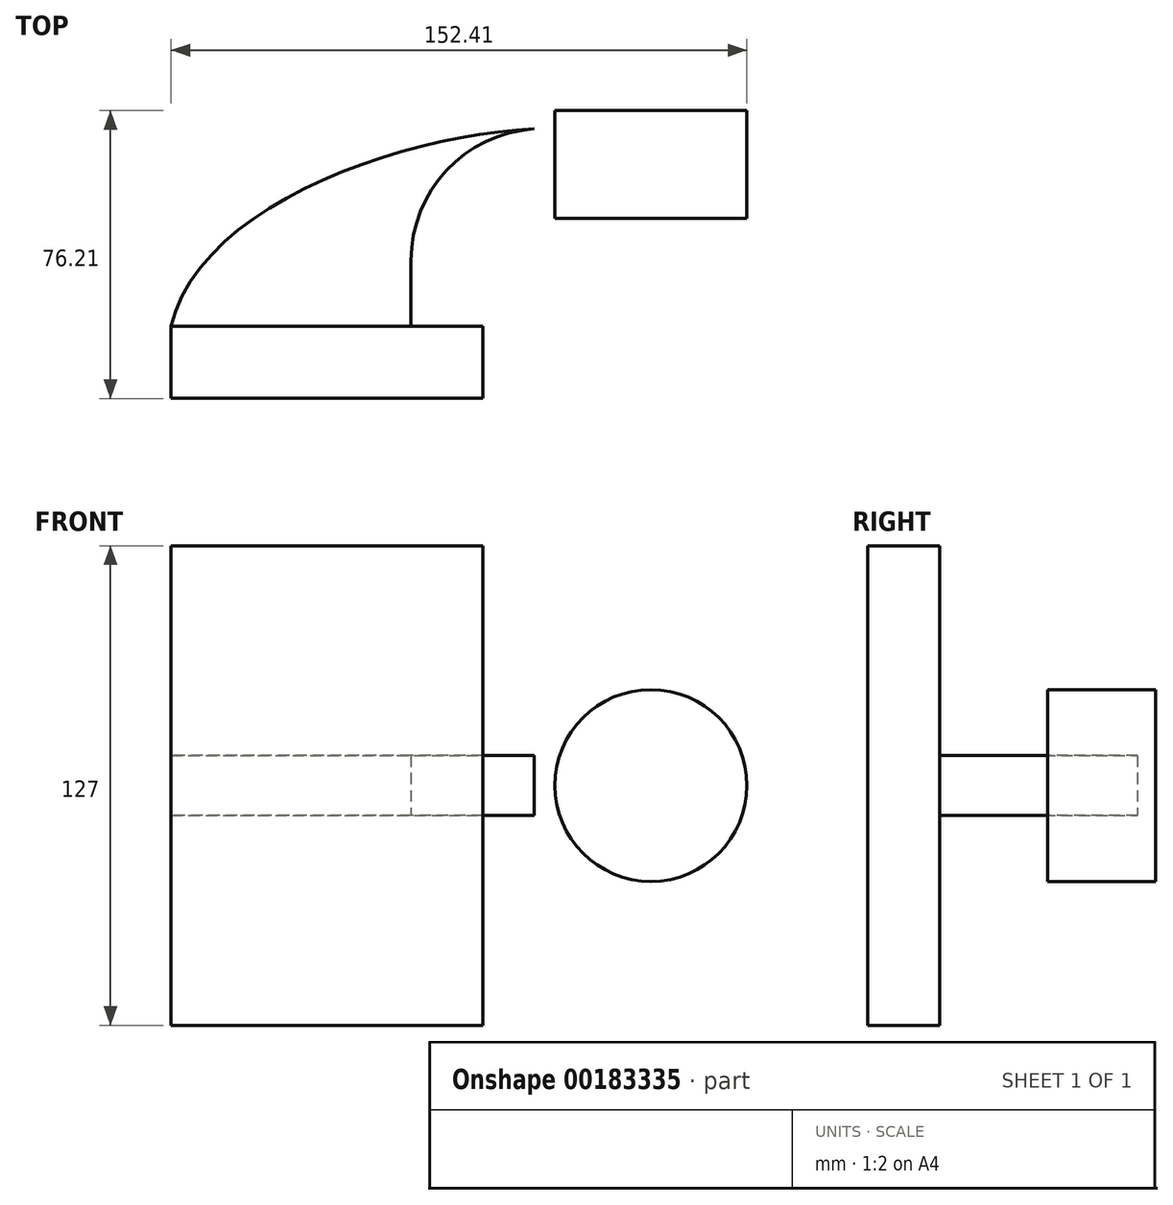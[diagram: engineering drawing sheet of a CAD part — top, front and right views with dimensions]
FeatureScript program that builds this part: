
annotation { "Feature Type Name" : "Feature", "Feature Type Description" : "" }
export const myFeature = defineFeature(function(context is Context, id is Id, definition is map)
    precondition{}
    {
        {
            var Q0;
            Q0=qCreatedBy(makeId("Top.planeOp"),FACE);
            var sketch = newSketch(context, id + "F0", { "sketchPlane" : qUnion([Q0])});
            skLineSegment(sketch, "E0.bottom", {"start": v(41.27, 9.53) * mm, "end": v(-41.28, 9.53) * mm});
            skLineSegment(sketch, "E0.top", {"start": v(41.28, -9.52) * mm, "end": v(-41.27, -9.52) * mm});
            skLineSegment(sketch, "E0.left", {"start": v(41.27, 9.53) * mm, "end": v(41.28, -9.52) * mm});
            skLineSegment(sketch, "E0.right", {"start": v(-41.28, 9.53) * mm, "end": v(-41.27, -9.52) * mm});
            skPoint(sketch, "E0.middle", {"position": v(0, 0) * mm});
            skLineSegment(sketch, "E1.bottom", {"start": v(111.12, 38.1) * mm, "end": v(60.32, 38.1) * mm});
            skLineSegment(sketch, "E1.top", {"start": v(111.12, 66.68) * mm, "end": v(60.32, 66.68) * mm});
            skLineSegment(sketch, "E1.left", {"start": v(111.12, 38.1) * mm, "end": v(111.12, 66.68) * mm});
            skLineSegment(sketch, "E1.right", {"start": v(60.32, 38.1) * mm, "end": v(60.32, 66.68) * mm});
            skPoint(sketch, "E1.middle", {"position": v(85.72, 52.39) * mm});
            skLineSegment(sketch, "E2", {"start": v(41.27, 9.53) * mm, "end": v(41.27, 27) * mm});
            skArc(sketch, "E3", {"start": v(57.15, 42.88) * mm, "mid": v(45.92, 38.23) * mm, "end": v(41.27, 27) * mm});
            skLineSegment(sketch, "E4", {"start": v(57.15, 42.88) * mm, "end": v(85.6, 42.88) * mm});
            skLineSegment(sketch, "E5.0", {"start": v(57.15, 61.93) * mm, "end": v(85.6, 61.93) * mm});
            skArc(sketch, "E5.1", {"start": v(57.15, 61.93) * mm, "mid": v(32.45, 51.7) * mm, "end": v(22.22, 27) * mm});
            skLineSegment(sketch, "E5.2", {"start": v(22.22, 9.53) * mm, "end": v(22.22, 27) * mm});
            skFitSpline(sketch, "E6", {"points": [v(-41.28, 9.53) * mm, v(57.15, 61.93) * mm], "startDerivative": vector(22.44, 98.86) * mm, "endDerivative": vector(104.12, 2.33) * mm});
            skLineSegment(sketch, "E7", {"start": v(85.72, 38.1) * mm, "end": v(85.72, 66.68) * mm});
            skSolve(sketch);
        }
        {
            var Q0;
            Q0=makeQuery(id+"F0.imprint","IMPRINT",FACE,{"disambiguationData":[TD([[makeQuery(id+"F0.imprint","IMPRINT",EDGE,{"derivedFrom":sQuery(id+"F0.wireOp",EDGE,"E0.top")}),-1.0]])]});
            extrude(context, id + "F1", {"entities" : qUnion([Q0]), "endBound" : BoundingType.SYMMETRIC, "depth" : 127 * mm});
        }
        {
            var Q0;
            {var subQ5=sQuery(id+"F0.wireOp",EDGE,"E2");Q0=makeQuery(id+"F0.imprint","IMPRINT",FACE,{"disambiguationData":[TD([[makeQuery(id+"F0.imprint","IMPRINT",EDGE,{"derivedFrom":subQ5}),1.0]])]});}
            var Q1;
            {var subQ1=sQuery(id+"F0.wireOp",EDGE,"E1.bottom");Q1=makeQuery(id+"F0.imprint","IMPRINT",FACE,{"disambiguationData":[TD([[makeQuery(id+"F0.imprint","IMPRINT",EDGE,{"derivedFrom":subQ1}),-1.0]])]});}
            extrude(context, id + "F2", {"entities" : qUnion([Q0, Q1]), "operationType" : NewBodyOperationType.REMOVE, "endBound" : BoundingType.SYMMETRIC, "depth" : 50.8 * mm});
        }
        {
            var Q0;
            {var subQ3=sQuery(id+"F0.wireOp",EDGE,"E5.2");Q0=makeQuery(id+"F0.imprint","IMPRINT",FACE,{"disambiguationData":[TD([[makeQuery(id+"F0.imprint","IMPRINT",EDGE,{"derivedFrom":subQ3}),1.0]])]});}
            extrude(context, id + "F3", {"entities" : qUnion([Q0]), "endBound" : BoundingType.SYMMETRIC, "depth" : 15.88 * mm});
        }
        {
            var Q0;
            {var subQ0=sQuery(id+"F0.wireOp",EDGE,"E1.left");Q0=makeQuery(id+"F0.imprint","IMPRINT",FACE,{"disambiguationData":[TD([[makeQuery(id+"F0.imprint","IMPRINT",EDGE,{"derivedFrom":subQ0}),1.0]])]});}
            var Q1;
            Q1=sQuery(id+"F0.wireOp",EDGE,"E7");
            revolve(context, id + "F4", {"operationType" : NewBodyOperationType.ADD, "entities" : qUnion([Q0]), "axis" : qUnion([Q1]), "revolveType" : RevolveType.FULL});
        }
    });
